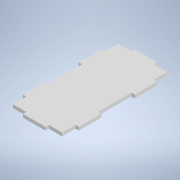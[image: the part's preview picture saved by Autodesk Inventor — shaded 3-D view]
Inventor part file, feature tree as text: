
AUTODESK INVENTOR PART (.ipt)
format: ipt  version: 2020.3 (Build 243373000, 373)  size: 156,672 bytes
history: native  units: mm
features: extrude x2, sketch x2
ambient origin geometry x8: Origin, YZ Plane, XZ Plane, XY Plane, X Axis, Y Axis, Z Axis, Center Point
bodies: Solid1 (feature_tree)
feature tree (4):
  extrude  "Base"  Depth=50.0mm
  extrude  "Tabs"  Depth=15.0mm
  sketch  "Sketch1"  dims[d0=100.0mm d1=50.0mm]
  sketch  "Sketch2"  dims[d2=3.0mm d3=0.0mm d10=15.0mm d11=15.0mm d12=20.0mm d13=20.0mm d14=30.0mm d15=3.0mm d16=0.0mm d17=0.0mm d21=3.0mm d22=10.0mm]
